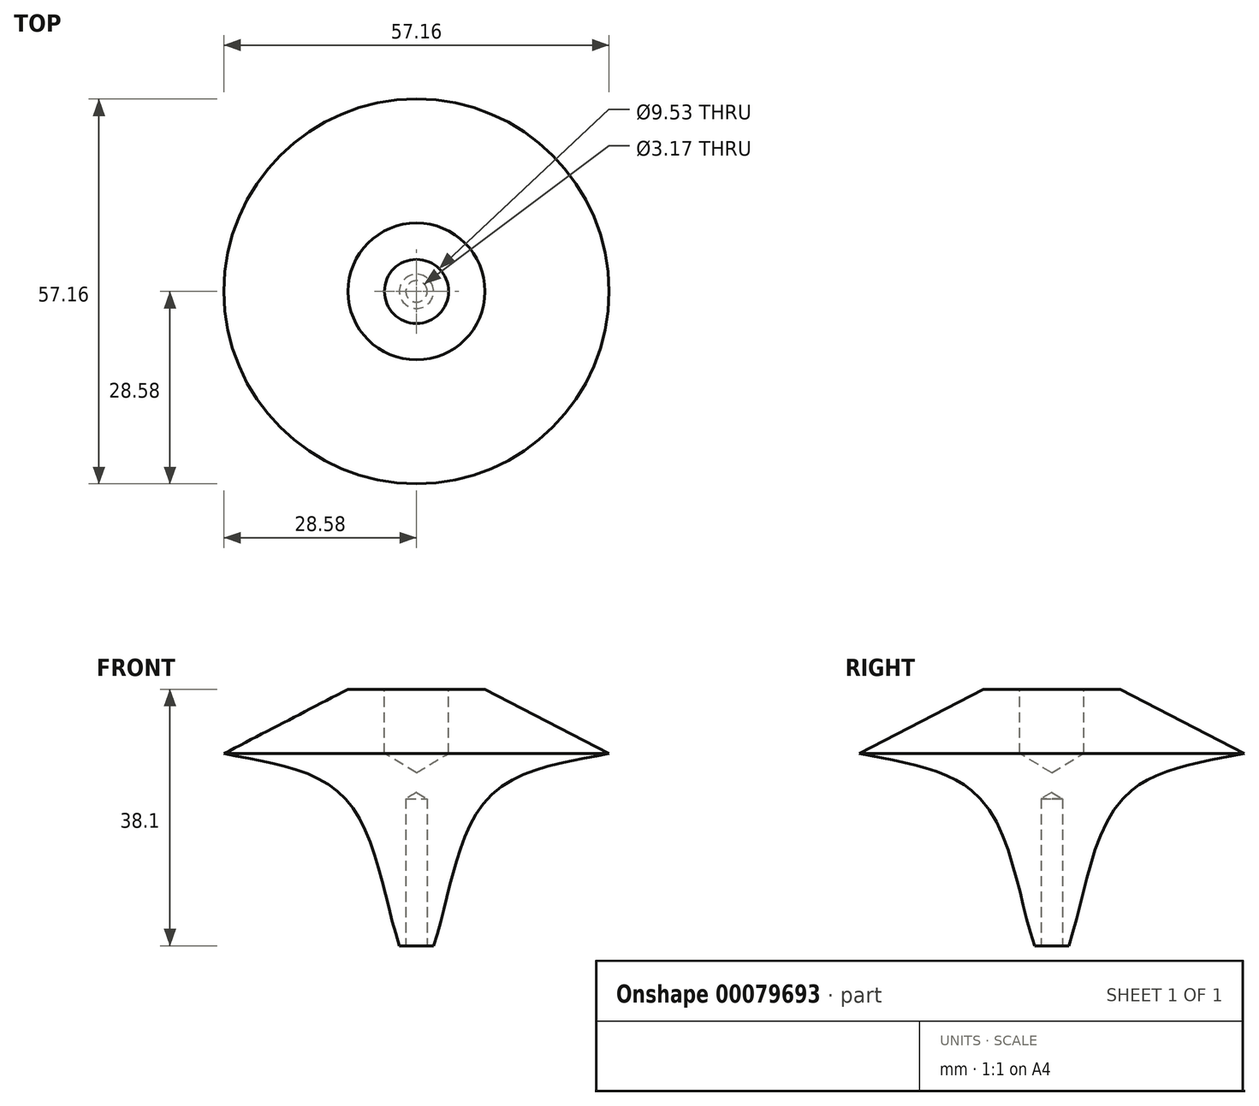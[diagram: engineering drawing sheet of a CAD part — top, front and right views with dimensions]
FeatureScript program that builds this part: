
annotation { "Feature Type Name" : "Feature", "Feature Type Description" : "" }
export const myFeature = defineFeature(function(context is Context, id is Id, definition is map)
    precondition{}
    {
        {
            var Q0;
            Q0=qCreatedBy(makeId("Front.planeOp"),FACE);
            var sketch = newSketch(context, id + "F0", { "sketchPlane" : qUnion([Q0])});
            skPoint(sketch, "E0.end.orphan", {"position": v(0, -28.54) * mm});
            skLineSegment(sketch, "E1", {"start": v(0, -28.54) * mm, "end": v(0, 9.56) * mm});
            skLineSegment(sketch, "E2", {"start": v(0, 0) * mm, "end": v(-28.58, 0) * mm});
            skLineSegment(sketch, "E3", {"start": v(0, 9.56) * mm, "end": v(-10.16, 9.56) * mm});
            skLineSegment(sketch, "E4", {"start": v(-28.58, 0) * mm, "end": v(-10.16, 9.56) * mm});
            skLineSegment(sketch, "E5", {"start": v(0, -28.54) * mm, "end": v(-2.54, -28.54) * mm});
            skFitSpline(sketch, "E6", {"points": [v(-28.58, 0) * mm, v(-10.55, -6.7) * mm, v(-2.54, -28.54) * mm], "startDerivative": vector(40.77, -8.2) * mm, "endDerivative": vector(13.24, -39.96) * mm});
            skSolve(sketch);
        }
        {
            var Q0;
            Q0 = qSketchRegion(id + "F0", true);
            var Q1;
            Q1=sQuery(id+"F0.wireOp",EDGE,"E1");
            revolve(context, id + "F1", {"entities" : qUnion([Q0]), "axis" : qUnion([Q1]), "revolveType" : RevolveType.FULL});
        }
        {
            var Q0;
            Q0=makeQuery(id+"F1.opRevolve","SWEPT_FACE",FACE,{"disambiguationData":[OSD([sQuery(id+"F0.wireOp",EDGE,"E3")])]});
            var sketch = newSketch(context, id + "F2", { "sketchPlane" : qUnion([Q0])});
            skCircle(sketch, "E7", {"center": v(0, 0) * mm, "radius": 2.32 * mm});
            skSolve(sketch);
        }
        {
            var Q0;
            Q0=sQuery(id+"F2.wireOp",VERTEX,"E7.center");
            var Q1;
            Q1=makeQuery(id+"F1.opRevolve","SWEPT_BODY",BODY,{"disambiguationData":[OSD([sQuery(id+"F0.wireOp",EDGE,"E1"),sQuery(id+"F0.wireOp",EDGE,"E3"),sQuery(id+"F0.wireOp",EDGE,"E4"),sQuery(id+"F0.wireOp",EDGE,"E5"),sQuery(id+"F0.wireOp",EDGE,"E6")])]});
            hole(context, id + "F3", {"style" : HoleStyle.SIMPLE, "endStyle" : HoleEndStyle.BLIND, "holeDiameter" : 9.52 * mm, "holeDepth" : 9.52 * mm, "locations" : qUnion([Q0]), "scope" : qUnion([Q1])});
        }
        {
            var Q0;
            Q0=makeQuery(id+"F1.opRevolve","SWEPT_FACE",FACE,{"disambiguationData":[OSD([sQuery(id+"F0.wireOp",EDGE,"E5")])]});
            var sketch = newSketch(context, id + "F4", { "sketchPlane" : qUnion([Q0])});
            skCircle(sketch, "E8", {"center": v(0, 0) * mm, "radius": 1.32 * mm});
            skSolve(sketch);
        }
        {
            var Q0;
            Q0=sQuery(id+"F4.wireOp",VERTEX,"E8.center");
            var Q1;
            Q1=makeQuery(id+"F1.opRevolve","SWEPT_BODY",BODY,{"disambiguationData":[OSD([sQuery(id+"F0.wireOp",EDGE,"E1"),sQuery(id+"F0.wireOp",EDGE,"E3"),sQuery(id+"F0.wireOp",EDGE,"E4"),sQuery(id+"F0.wireOp",EDGE,"E5"),sQuery(id+"F0.wireOp",EDGE,"E6")])]});
            hole(context, id + "F5", {"style" : HoleStyle.SIMPLE, "endStyle" : HoleEndStyle.BLIND, "holeDiameter" : 3.17 * mm, "holeDepth" : 21.84 * mm, "locations" : qUnion([Q0]), "scope" : qUnion([Q1])});
        }
    });
